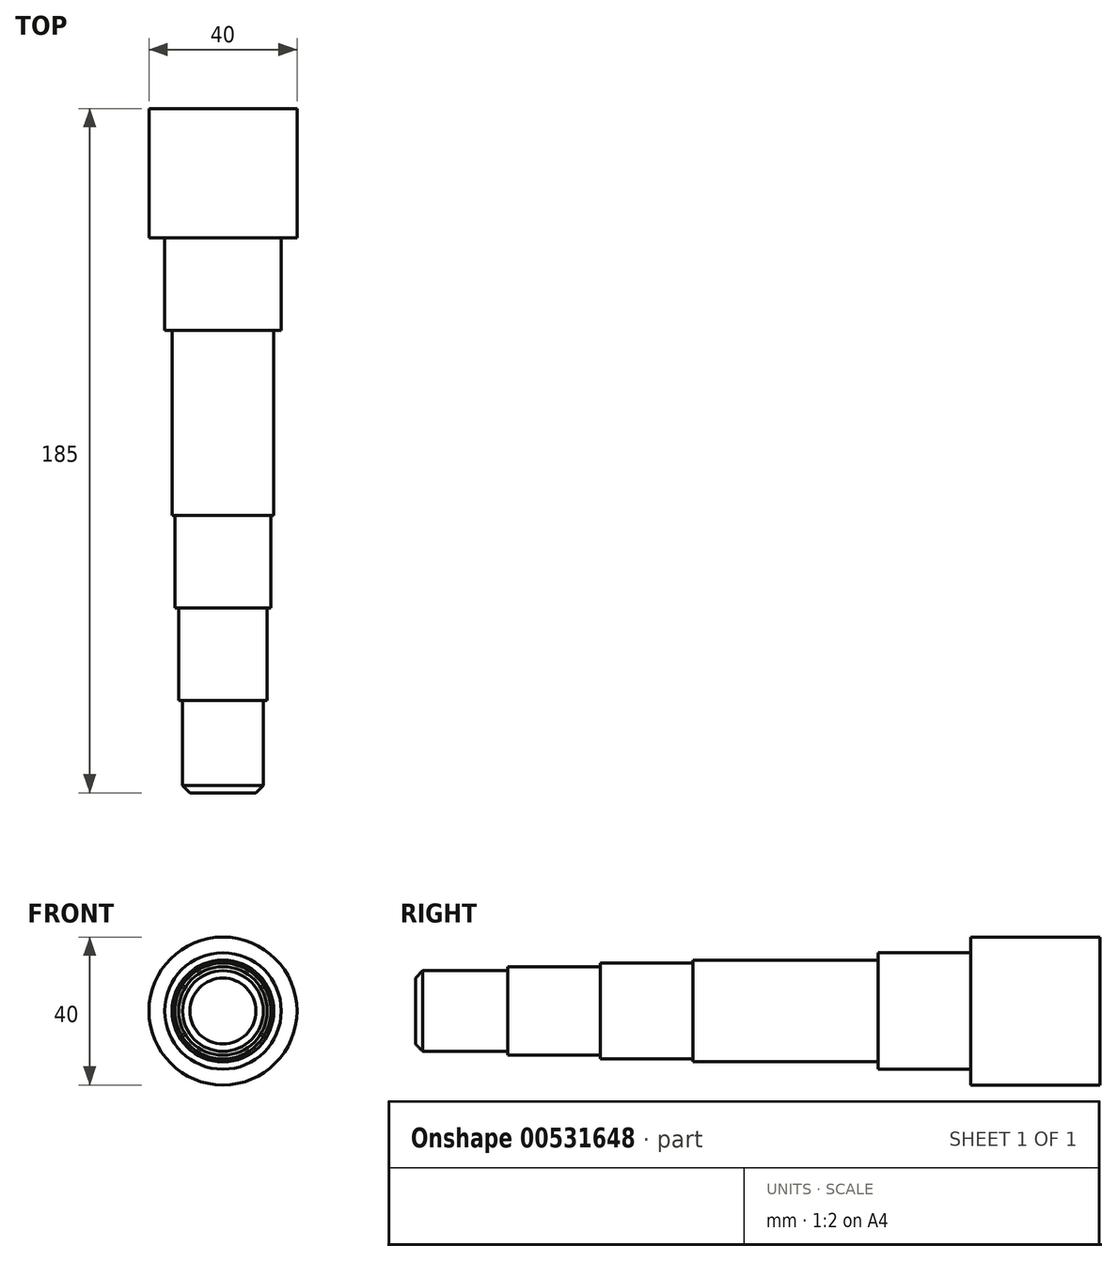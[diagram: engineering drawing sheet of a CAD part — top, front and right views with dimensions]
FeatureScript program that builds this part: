
annotation { "Feature Type Name" : "Feature", "Feature Type Description" : "" }
export const myFeature = defineFeature(function(context is Context, id is Id, definition is map)
    precondition{}
    {
        {
            var Q0;
            Q0=qCreatedBy(makeId("Front.planeOp"),FACE);
            var sketch = newSketch(context, id + "F0", { "sketchPlane" : qUnion([Q0])});
            skCircle(sketch, "E0", {"center": v(0, 0) * mm, "radius": 20 * mm});
            skSolve(sketch);
        }
        {
            var Q0;
            Q0=makeQuery(id+"F0.imprint","IMPRINT",FACE,{"disambiguationData":[TD([[makeQuery(id+"F0.imprint","IMPRINT",EDGE,{"derivedFrom":sQuery(id+"F0.wireOp",EDGE,"E0")}),1.0]])]});
            extrude(context, id + "F1", {"entities" : qUnion([Q0]), "depth" : 35 * mm, "offsetDistance" : 25 * mm});
        }
        {
            var Q0;
            Q0=makeQuery(id+"F1.opExtrude","CAP_FACE",FACE,{"disambiguationData":[OSD([sQuery(id+"F0.wireOp",EDGE,"E0")])],"isStart":false});
            cPlane(context, id + "F2", {"entities" : qUnion([Q0]), "cplaneType" : CPlaneType.OFFSET, "offset" : 0 * mm, "width" : 150 * mm, "height" : 150 * mm});
        }
        {
            var Q0;
            Q0=qCreatedBy(id+"F2.planeOp",FACE);
            var sketch = newSketch(context, id + "F3", { "sketchPlane" : qUnion([Q0])});
            skCircle(sketch, "E1", {"center": v(0, 0) * mm, "radius": 15.75 * mm});
            skSolve(sketch);
        }
        {
            var Q0;
            Q0=makeQuery(id+"F3.imprint","IMPRINT",FACE,{"disambiguationData":[TD([[makeQuery(id+"F3.imprint","IMPRINT",EDGE,{"derivedFrom":sQuery(id+"F3.wireOp",EDGE,"E1")}),1.0]])]});
            extrude(context, id + "F4", {"entities" : qUnion([Q0]), "operationType" : NewBodyOperationType.ADD, "depth" : 25 * mm, "offsetDistance" : 25 * mm});
        }
        {
            var Q0;
            Q0=makeQuery(id+"F4.opExtrude","CAP_FACE",FACE,{"disambiguationData":[OSD([sQuery(id+"F3.wireOp",EDGE,"E1")])],"isStart":false});
            cPlane(context, id + "F5", {"entities" : qUnion([Q0]), "cplaneType" : CPlaneType.OFFSET, "offset" : 0 * mm, "width" : 150 * mm, "height" : 150 * mm});
        }
        {
            var Q0;
            Q0=qCreatedBy(id+"F5.planeOp",FACE);
            var sketch = newSketch(context, id + "F6", { "sketchPlane" : qUnion([Q0])});
            skCircle(sketch, "E2", {"center": v(0, 0) * mm, "radius": 13.75 * mm});
            skSolve(sketch);
        }
        {
            var Q0;
            Q0=makeQuery(id+"F6.imprint","IMPRINT",FACE,{"disambiguationData":[TD([[makeQuery(id+"F6.imprint","IMPRINT",EDGE,{"derivedFrom":sQuery(id+"F6.wireOp",EDGE,"E2")}),1.0]])]});
            extrude(context, id + "F7", {"entities" : qUnion([Q0]), "operationType" : NewBodyOperationType.ADD, "depth" : 50 * mm, "offsetDistance" : 25 * mm});
        }
        {
            var Q0;
            Q0=makeQuery(id+"F7.opExtrude","CAP_FACE",FACE,{"disambiguationData":[OSD([sQuery(id+"F6.wireOp",EDGE,"E2")])],"isStart":false});
            var sketch = newSketch(context, id + "F8", { "sketchPlane" : qUnion([Q0])});
            skPoint(sketch, "E3.center.orphan", {"position": v(0, 0) * mm});
            skCircle(sketch, "E4", {"center": v(0, 0) * mm, "radius": 12.97 * mm});
            skSolve(sketch);
        }
        {
            var Q0;
            Q0=makeQuery(id+"F8.imprint","IMPRINT",FACE,{"disambiguationData":[TD([[makeQuery(id+"F8.imprint","IMPRINT",EDGE,{"derivedFrom":sQuery(id+"F8.wireOp",EDGE,"E4")}),1.0]])]});
            extrude(context, id + "F9", {"entities" : qUnion([Q0]), "operationType" : NewBodyOperationType.ADD, "depth" : 25 * mm, "offsetDistance" : 25 * mm});
        }
        {
            var Q0;
            Q0=makeQuery(id+"F9.opExtrude","CAP_FACE",FACE,{"disambiguationData":[OSD([sQuery(id+"F8.wireOp",EDGE,"E4")])],"isStart":false});
            var sketch = newSketch(context, id + "F10", { "sketchPlane" : qUnion([Q0])});
            skCircle(sketch, "E5", {"center": v(0, 0) * mm, "radius": 11.97 * mm});
            skSolve(sketch);
        }
        {
            var Q0;
            Q0 = qSketchRegion(id + "F10", true);
            extrude(context, id + "F11", {"entities" : qUnion([Q0]), "operationType" : NewBodyOperationType.ADD, "depth" : 25 * mm, "offsetDistance" : 25 * mm});
        }
        {
            var Q0;
            Q0=makeQuery(id+"F11.opExtrude","CAP_FACE",FACE,{"disambiguationData":[OSD([sQuery(id+"F10.wireOp",EDGE,"E5")])],"isStart":false});
            var sketch = newSketch(context, id + "F12", { "sketchPlane" : qUnion([Q0])});
            skCircle(sketch, "E6", {"center": v(0, 0) * mm, "radius": 10.9 * mm});
            skSolve(sketch);
        }
        {
            var Q0;
            Q0 = qSketchRegion(id + "F12", true);
            extrude(context, id + "F13", {"entities" : qUnion([Q0]), "operationType" : NewBodyOperationType.ADD, "depth" : 25 * mm, "offsetDistance" : 25 * mm});
        }
        {
            var Q0;
            Q0=makeQuery(id+"F13.opExtrude","CAP_EDGE",EDGE,{"disambiguationData":[OSD([sQuery(id+"F12.wireOp",EDGE,"E6")])],"isStart":false});
            chamfer(context, id + "F14", {"entities" : qUnion([Q0]), "width" : 2 * mm, "tangentPropagation" : true});
        }
    });
